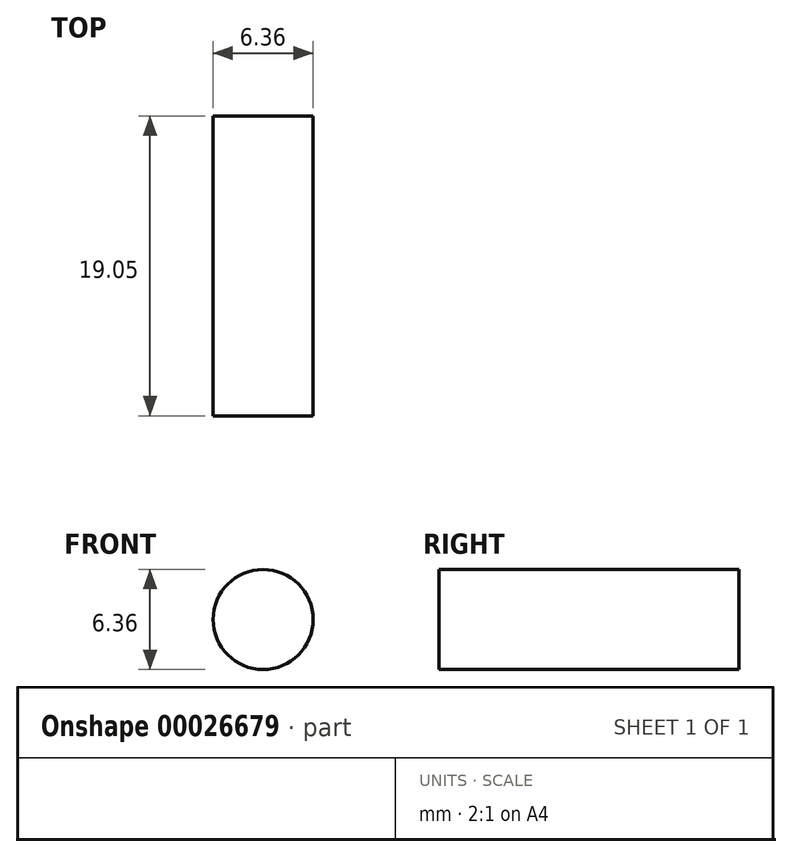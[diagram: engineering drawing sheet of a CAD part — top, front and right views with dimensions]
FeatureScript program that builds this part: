
annotation { "Feature Type Name" : "Feature", "Feature Type Description" : "" }
export const myFeature = defineFeature(function(context is Context, id is Id, definition is map)
    precondition{}
    {
        {
            var Q0;
            Q0=qCreatedBy(makeId("Front.planeOp"),FACE);
            var sketch = newSketch(context, id + "F0", { "sketchPlane" : qUnion([Q0])});
            skCircle(sketch, "E0", {"center": v(0, 0) * mm, "radius": 3.18 * mm});
            skSolve(sketch);
        }
        {
            var Q0;
            Q0=makeQuery(id+"F0.imprint","IMPRINT",FACE,{"disambiguationData":[TD([[makeQuery(id+"F0.imprint","IMPRINT",EDGE,{"derivedFrom":sQuery(id+"F0.wireOp",EDGE,"E0")}),1.0]])]});
            extrude(context, id + "F1", {"entities" : qUnion([Q0]), "depth" : 19.05 * mm});
        }
    });
